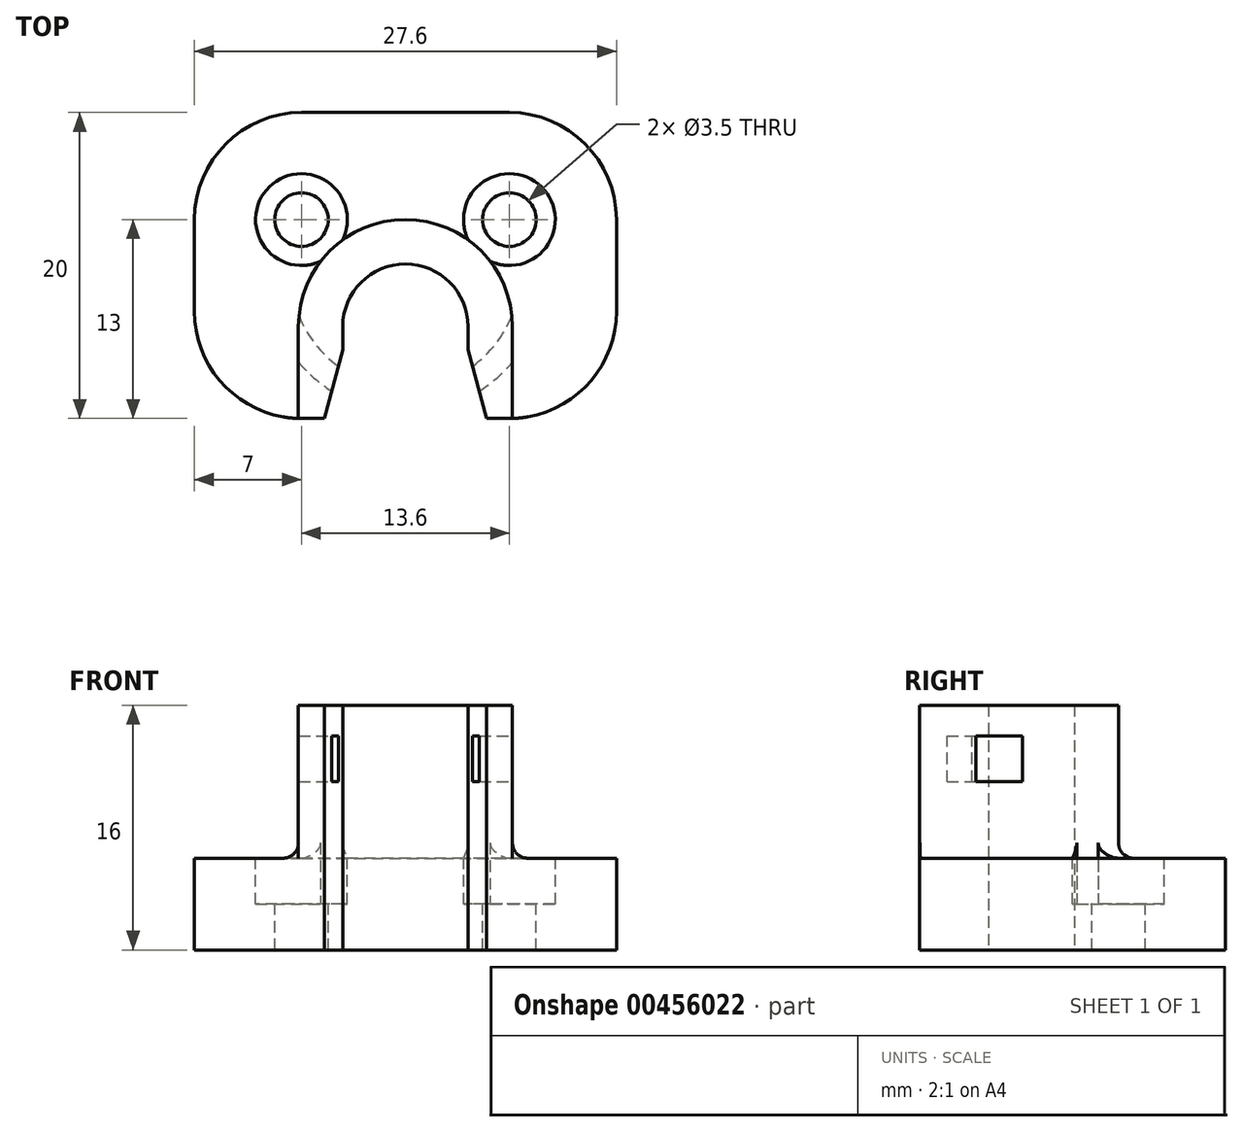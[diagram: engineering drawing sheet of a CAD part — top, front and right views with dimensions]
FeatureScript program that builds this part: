
annotation { "Feature Type Name" : "Feature", "Feature Type Description" : "" }
export const myFeature = defineFeature(function(context is Context, id is Id, definition is map)
    precondition{}
    {
        {
            var Q0;
            Q0=qCreatedBy(makeId("Top.planeOp"),FACE);
            var sketch = newSketch(context, id + "F0", { "sketchPlane" : qUnion([Q0])});
            skLineSegment(sketch, "E0", {"start": v(0, 14) * mm, "end": v(-6.8, 14) * mm});
            skLineSegment(sketch, "E1", {"start": v(-13.8, 7) * mm, "end": v(-13.8, 1) * mm});
            skLineSegment(sketch, "E2", {"start": v(-6.8, -6) * mm, "end": v(0, -6) * mm});
            skLineSegment(sketch, "E3", {"start": v(0, 21) * mm, "end": v(0, -14.7) * mm, "construction": true});
            skPoint(sketch, "E4.visualSharp", {"position": v(-13.8, 14) * mm});
            skArc(sketch, "E4.filletArc", {"start": v(-6.8, 14) * mm, "mid": v(-11.75, 11.95) * mm, "end": v(-13.8, 7) * mm});
            skPoint(sketch, "E5.visualSharp", {"position": v(-13.8, -6) * mm});
            skArc(sketch, "E5.filletArc", {"start": v(-13.8, 1) * mm, "mid": v(-11.75, -3.95) * mm, "end": v(-6.8, -6) * mm});
            skLineSegment(sketch, "E6.MirrorCS", {"start": v(0, 14) * mm, "end": v(6.8, 14) * mm});
            skLineSegment(sketch, "E7.MirrorCS", {"start": v(6.8, -6) * mm, "end": v(0, -6) * mm});
            skLineSegment(sketch, "E8.MirrorCS", {"start": v(13.8, 7) * mm, "end": v(13.8, 1) * mm});
            skPoint(sketch, "E9.MirrorP", {"position": v(13.8, -6) * mm});
            skArc(sketch, "E10.MirrorCS", {"start": v(13.8, 1) * mm, "mid": v(11.75, -3.95) * mm, "end": v(6.8, -6) * mm});
            skPoint(sketch, "E11.MirrorP", {"position": v(13.8, 14) * mm});
            skArc(sketch, "E12.MirrorCS", {"start": v(6.8, 14) * mm, "mid": v(11.75, 11.95) * mm, "end": v(13.8, 7) * mm});
            skSolve(sketch);
        }
        {
            var Q0;
            Q0 = qSketchRegion(id + "F0", true);
            extrude(context, id + "F1", {"entities" : qUnion([Q0]), "depth" : 6 * mm});
        }
        {
            var Q0;
            Q0=makeQuery(id+"F1.opExtrude","CAP_FACE",FACE,{"disambiguationData":[OSD([sQuery(id+"F0.wireOp",EDGE,"E0"),sQuery(id+"F0.wireOp",EDGE,"E1"),sQuery(id+"F0.wireOp",EDGE,"E2"),sQuery(id+"F0.wireOp",EDGE,"E4.filletArc"),sQuery(id+"F0.wireOp",EDGE,"E5.filletArc"),sQuery(id+"F0.wireOp",EDGE,"E6.MirrorCS"),sQuery(id+"F0.wireOp",EDGE,"E7.MirrorCS"),sQuery(id+"F0.wireOp",EDGE,"E8.MirrorCS"),sQuery(id+"F0.wireOp",EDGE,"E10.MirrorCS"),sQuery(id+"F0.wireOp",EDGE,"E12.MirrorCS")])],"isStart":false});
            var sketch = newSketch(context, id + "F2", { "sketchPlane" : qUnion([Q0])});
            skPoint(sketch, "E13.0", {"position": v(-6.8, 7) * mm});
            skPoint(sketch, "E14.0", {"position": v(6.8, 7) * mm});
            skSolve(sketch);
        }
        {
            var Q0;
            Q0=sQuery(id+"F2.wireOp",VERTEX,"E13.0");
            var Q1;
            Q1=sQuery(id+"F2.wireOp",VERTEX,"E14.0");
            var Q2;
            Q2=makeQuery(id+"F1.opExtrude","SWEPT_BODY",BODY,{"disambiguationData":[OSD([sQuery(id+"F0.wireOp",EDGE,"E0"),sQuery(id+"F0.wireOp",EDGE,"E1"),sQuery(id+"F0.wireOp",EDGE,"E2"),sQuery(id+"F0.wireOp",EDGE,"E4.filletArc"),sQuery(id+"F0.wireOp",EDGE,"E5.filletArc"),sQuery(id+"F0.wireOp",EDGE,"E6.MirrorCS"),sQuery(id+"F0.wireOp",EDGE,"E7.MirrorCS"),sQuery(id+"F0.wireOp",EDGE,"E8.MirrorCS"),sQuery(id+"F0.wireOp",EDGE,"E10.MirrorCS"),sQuery(id+"F0.wireOp",EDGE,"E12.MirrorCS")])]});
            hole(context, id + "F3", {"style" : HoleStyle.C_BORE, "endStyle" : HoleEndStyle.THROUGH, "holeDiameter" : 3.5 * mm, "cBoreDiameter" : 6 * mm, "cBoreDepth" : 3 * mm, "isTappedThrough" : true, "tappedDepth" : 12 * mm, "tapClearance" : 3, "startFromSketch" : true, "locations" : qUnion([Q0, Q1]), "scope" : qUnion([Q2])});
        }
        {
            var Q0;
            Q0=qCreatedBy(makeId("Top.planeOp"),FACE);
            var sketch = newSketch(context, id + "F4", { "sketchPlane" : qUnion([Q0])});
            skArc(sketch, "E15", {"start": v(7, 0) * mm, "mid": v(0, 7) * mm, "end": v(-7, 0) * mm});
            skLineSegment(sketch, "E16", {"start": v(-7, 0) * mm, "end": v(-7, -6) * mm});
            skLineSegment(sketch, "E17", {"start": v(7, 0) * mm, "end": v(7, -6) * mm});
            skLineSegment(sketch, "E18", {"start": v(-7, -6) * mm, "end": v(7, -6) * mm});
            skSolve(sketch);
        }
        {
            var Q0;
            Q0 = qSketchRegion(id + "F4", true);
            extrude(context, id + "F5", {"entities" : qUnion([Q0]), "operationType" : NewBodyOperationType.ADD, "depth" : 16 * mm});
        }
        {
            var Q0;
            Q0=qCreatedBy(makeId("Top.planeOp"),FACE);
            var sketch = newSketch(context, id + "F6", { "sketchPlane" : qUnion([Q0])});
            skArc(sketch, "E19", {"start": v(0, 4.1) * mm, "mid": v(-2.9, 2.9) * mm, "end": v(-4.1, 0) * mm});
            skLineSegment(sketch, "E20", {"start": v(-4.1, 0) * mm, "end": v(-4.1, -1.5) * mm});
            skLineSegment(sketch, "E21", {"start": v(-4.1, -1.5) * mm, "end": v(-5.3, -6) * mm});
            skLineSegment(sketch, "E22", {"start": v(-5.3, -6) * mm, "end": v(0, -6) * mm});
            skLineSegment(sketch, "E23", {"start": v(0, 6.06) * mm, "end": v(0, -9.17) * mm, "construction": true});
            skLineSegment(sketch, "E24.MirrorCS", {"start": v(5.3, -6) * mm, "end": v(0, -6) * mm});
            skLineSegment(sketch, "E25.MirrorCS", {"start": v(4.1, 0) * mm, "end": v(4.1, -1.5) * mm});
            skLineSegment(sketch, "E26.MirrorCS", {"start": v(4.1, -1.5) * mm, "end": v(5.3, -6) * mm});
            skArc(sketch, "E27.MirrorCS", {"start": v(0, 4.1) * mm, "mid": v(2.9, 2.9) * mm, "end": v(4.1, 0) * mm});
            skSolve(sketch);
        }
        {
            var Q0;
            Q0 = qSketchRegion(id + "F6", true);
            extrude(context, id + "F7", {"entities" : qUnion([Q0]), "operationType" : NewBodyOperationType.REMOVE, "endBound" : BoundingType.THROUGH_ALL, "depth" : 25 * mm});
        }
        {
            var Q0;
            Q0=makeQuery(id+"F5.opExtrude","CAP_FACE",FACE,{"disambiguationData":[OSD([sQuery(id+"F4.wireOp",EDGE,"E15"),sQuery(id+"F4.wireOp",EDGE,"E16"),sQuery(id+"F4.wireOp",EDGE,"E17"),sQuery(id+"F4.wireOp",EDGE,"E18")])],"isStart":false});
            cPlane(context, id + "F8", {"entities" : qUnion([Q0]), "cplaneType" : CPlaneType.OFFSET, "offset" : 2 * mm, "oppositeDirection" : true, "width" : 150 * mm, "height" : 150 * mm});
        }
        {
            var Q0;
            Q0=qCreatedBy(id+"F8.planeOp",FACE);
            var sketch = newSketch(context, id + "F9", { "sketchPlane" : qUnion([Q0])});
            skCircle(sketch, "E28", {"center": v(0, 0) * mm, "radius": 4 * mm, "construction": true});
            skArc(sketch, "E29", {"start": v(-6.96, 0.71) * mm, "mid": v(-5.91, -1.12) * mm, "end": v(-4.39, -2.58) * mm});
            skArc(sketch, "E30.0", {"start": v(-7, -2.31) * mm, "mid": v(-5.99, -3.35) * mm, "end": v(-4.83, -4.21) * mm});
            skLineSegment(sketch, "E31.0", {"start": v(-4.83, -4.21) * mm, "end": v(-4.39, -2.58) * mm});
            skArc(sketch, "E32.0", {"start": v(-6.96, 0.71) * mm, "mid": v(-7, 0.36) * mm, "end": v(-7, 0) * mm});
            skLineSegment(sketch, "E33.0", {"start": v(-7, 0) * mm, "end": v(-7, -2.31) * mm});
            skPoint(sketch, "E34.orphan", {"position": v(7, 0) * mm});
            skPoint(sketch, "E35.orphan", {"position": v(-5.3, -6) * mm});
            skPoint(sketch, "E36.orphan", {"position": v(-4.1, -1.5) * mm});
            skPoint(sketch, "E37.orphan", {"position": v(-7, -6) * mm});
            skLineSegment(sketch, "E38.MirrorCS", {"start": v(4.83, -4.21) * mm, "end": v(4.39, -2.58) * mm});
            skLineSegment(sketch, "E39.MirrorCS", {"start": v(7, 0) * mm, "end": v(7, -2.31) * mm});
            skArc(sketch, "E40.MirrorCS", {"start": v(6.96, 0.71) * mm, "mid": v(5.91, -1.12) * mm, "end": v(4.39, -2.58) * mm});
            skArc(sketch, "E41.MirrorCS", {"start": v(7, -2.31) * mm, "mid": v(5.99, -3.35) * mm, "end": v(4.83, -4.21) * mm});
            skArc(sketch, "E42.MirrorCS", {"start": v(6.96, 0.71) * mm, "mid": v(7, 0.36) * mm, "end": v(7, 0) * mm});
            skSolve(sketch);
        }
        {
            var Q0;
            Q0 = qSketchRegion(id + "F9", true);
            extrude(context, id + "F10", {"entities" : qUnion([Q0]), "operationType" : NewBodyOperationType.REMOVE, "oppositeDirection" : true, "depth" : 3 * mm});
        }
        {
            var Q0;
            Q0=makeQuery(id+"F5.boolean.opBoolean","INTERSECT",EDGE,{"derivedFrom":[makeQuery(id+"F1.opExtrude","CAP_FACE",FACE,{"disambiguationData":[OSD([sQuery(id+"F0.wireOp",EDGE,"E0"),sQuery(id+"F0.wireOp",EDGE,"E1"),sQuery(id+"F0.wireOp",EDGE,"E2"),sQuery(id+"F0.wireOp",EDGE,"E4.filletArc"),sQuery(id+"F0.wireOp",EDGE,"E5.filletArc"),sQuery(id+"F0.wireOp",EDGE,"E6.MirrorCS"),sQuery(id+"F0.wireOp",EDGE,"E7.MirrorCS"),sQuery(id+"F0.wireOp",EDGE,"E8.MirrorCS"),sQuery(id+"F0.wireOp",EDGE,"E10.MirrorCS"),sQuery(id+"F0.wireOp",EDGE,"E12.MirrorCS")])],"isStart":false}),makeQuery(id+"F5.opExtrude","SWEPT_FACE",FACE,{"disambiguationData":[OSD([sQuery(id+"F4.wireOp",EDGE,"E16")])]})]});
            var Q1;
            Q1=makeQuery(id+"F5.boolean.opBoolean","INTERSECT",EDGE,{"disambiguationData":[OD(2.0)],"derivedFrom":[makeQuery(id+"F1.opExtrude","CAP_FACE",FACE,{"disambiguationData":[OSD([sQuery(id+"F0.wireOp",EDGE,"E0"),sQuery(id+"F0.wireOp",EDGE,"E1"),sQuery(id+"F0.wireOp",EDGE,"E2"),sQuery(id+"F0.wireOp",EDGE,"E4.filletArc"),sQuery(id+"F0.wireOp",EDGE,"E5.filletArc"),sQuery(id+"F0.wireOp",EDGE,"E6.MirrorCS"),sQuery(id+"F0.wireOp",EDGE,"E7.MirrorCS"),sQuery(id+"F0.wireOp",EDGE,"E8.MirrorCS"),sQuery(id+"F0.wireOp",EDGE,"E10.MirrorCS"),sQuery(id+"F0.wireOp",EDGE,"E12.MirrorCS")])],"isStart":false}),makeQuery(id+"F5.opExtrude","SWEPT_FACE",FACE,{"disambiguationData":[OSD([sQuery(id+"F4.wireOp",EDGE,"E15")])]})]});
            var Q2;
            Q2=makeQuery(id+"F5.boolean.opBoolean","INTERSECT",EDGE,{"derivedFrom":[makeQuery(id+"F1.opExtrude","CAP_FACE",FACE,{"disambiguationData":[OSD([sQuery(id+"F0.wireOp",EDGE,"E0"),sQuery(id+"F0.wireOp",EDGE,"E1"),sQuery(id+"F0.wireOp",EDGE,"E2"),sQuery(id+"F0.wireOp",EDGE,"E4.filletArc"),sQuery(id+"F0.wireOp",EDGE,"E5.filletArc"),sQuery(id+"F0.wireOp",EDGE,"E6.MirrorCS"),sQuery(id+"F0.wireOp",EDGE,"E7.MirrorCS"),sQuery(id+"F0.wireOp",EDGE,"E8.MirrorCS"),sQuery(id+"F0.wireOp",EDGE,"E10.MirrorCS"),sQuery(id+"F0.wireOp",EDGE,"E12.MirrorCS")])],"isStart":false}),makeQuery(id+"F5.opExtrude","SWEPT_FACE",FACE,{"disambiguationData":[OSD([sQuery(id+"F4.wireOp",EDGE,"E17")])]})]});
            fillet(context, id + "F11", {"entities" : qUnion([Q0, Q1, Q2]), "radius" : 1 * mm, "tangentPropagation" : true, "allowEdgeOverflow" : false});
        }
    });
